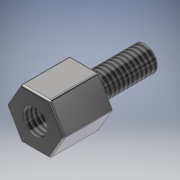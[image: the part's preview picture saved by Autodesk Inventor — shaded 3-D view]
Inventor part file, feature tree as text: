
AUTODESK INVENTOR PART (.ipt)
format: ipt  version: 2019.4 (Build 234330000, 330)  size: 156,672 bytes
history: native  units: mm
features: extrude x3, sketch x3, thread x2, fillet x1
ambient origin geometry x8: Origin, YZ Plane, XZ Plane, XY Plane, X Axis, Y Axis, Z Axis, Center Point
bodies: Solid1 (feature_tree)
feature tree (9):
  extrude  "Extrusion1"  Depth=5.0mm
  extrude  "Extrusion2"  Depth=2.5mm
  extrude  "Extrusion3"  TaperAngle=0.0deg  [1 undecoded]
  thread  "Thread1"  [1 undecoded]
  thread  "Thread2"  [1 undecoded]
  fillet  "Fillet1"  [1 undecoded]
  sketch  "Sketch1"  dims[d0=5.0mm d1=5.0mm]
  sketch  "Sketch2"  dims[d2=0.0mm d3=2.5mm]
  sketch  "Sketch3"  dims[d4=3.0mm d5=0.0mm d6=2.5mm d7=6.0mm d8=0.0mm d9=10.0mm d10=0.0mm d11=10.0mm d12=0.0mm d13=0.2mm d14=0.2mm]
note: 4 required parameter values undecoded (feature->parameter linkage not recoverable at this tier; creation-order binding heuristic only, values carry confidence <= 0.55)
